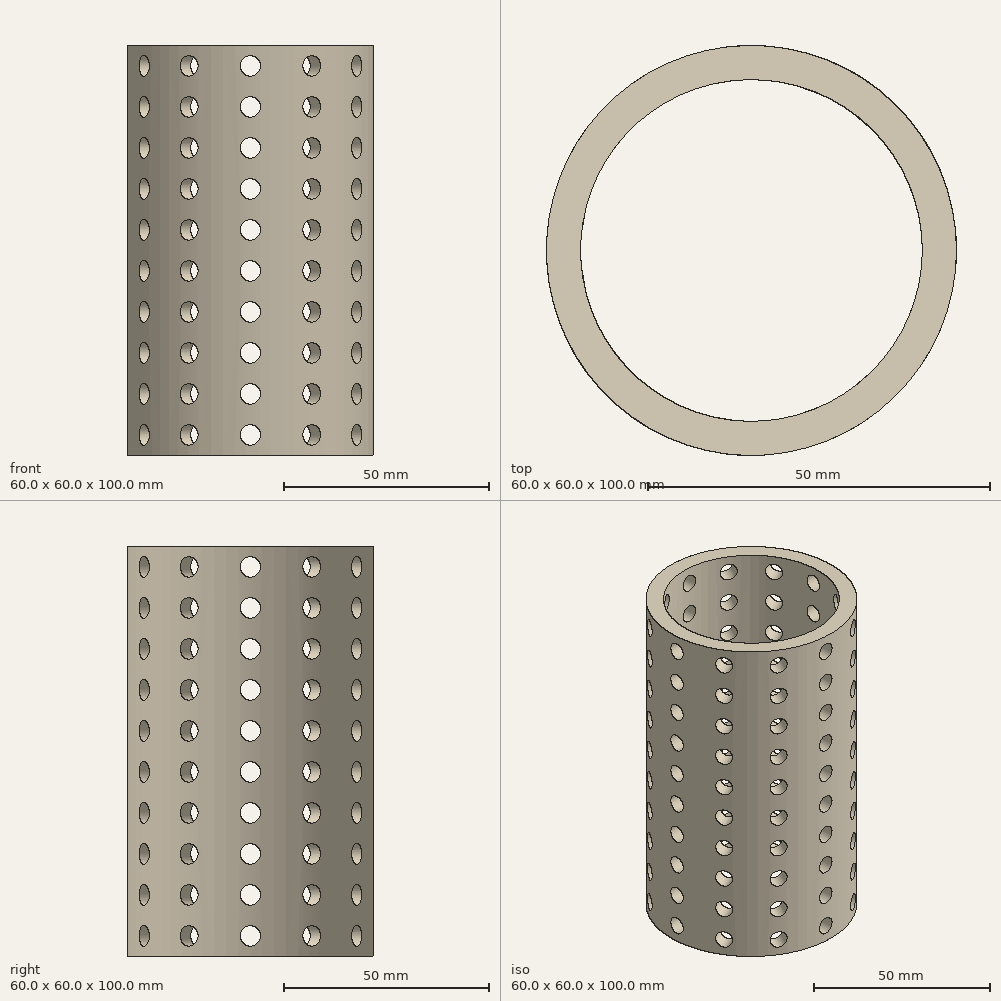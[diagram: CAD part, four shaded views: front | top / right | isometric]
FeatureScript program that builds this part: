
annotation { "Feature Type Name" : "Feature", "Feature Type Description" : "" }
export const myFeature = defineFeature(function(context is Context, id is Id, definition is map)
    precondition{}
    {
        {
            var Q0;
            Q0=qCreatedBy(makeId("Top.planeOp"),FACE);
            var sketch = newSketch(context, id + "F0", { "sketchPlane" : qUnion([Q0])});
            skCircle(sketch, "E0", {"center": v(0, 0) * mm, "radius": 30 * mm});
            skCircle(sketch, "E1", {"center": v(0, 0) * mm, "radius": 25 * mm});
            skSolve(sketch);
        }
        {
            var Q0;
            Q0=makeQuery(id+"F0.imprint","IMPRINT",FACE,{"disambiguationData":[TD([[makeQuery(id+"F0.imprint","IMPRINT",EDGE,{"derivedFrom":sQuery(id+"F0.wireOp",EDGE,"E0")}),1.0]])]});
            extrude(context, id + "F1", {"entities" : qUnion([Q0]), "depth" : 100 * mm});
        }
        {
            var Q0;
            Q0=qCreatedBy(makeId("Front.planeOp"),FACE);
            var sketch = newSketch(context, id + "F2", { "sketchPlane" : qUnion([Q0])});
            skCircle(sketch, "E2", {"center": v(0, 5) * mm, "radius": 2.5 * mm});
            skLineSegment(sketch, "E3", {"start": v(0, 0) * mm, "end": v(0, 99.71) * mm, "construction": true});
            skCircle(sketch, "E4.0.1.0", {"center": v(0, 15) * mm, "radius": 2.5 * mm});
            skCircle(sketch, "E4.0.2.0", {"center": v(0, 25) * mm, "radius": 2.5 * mm});
            skCircle(sketch, "E4.0.3.0", {"center": v(0, 35) * mm, "radius": 2.5 * mm});
            skCircle(sketch, "E4.0.4.0", {"center": v(0, 45) * mm, "radius": 2.5 * mm});
            skCircle(sketch, "E4.0.5.0", {"center": v(0, 55) * mm, "radius": 2.5 * mm});
            skCircle(sketch, "E4.0.6.0", {"center": v(0, 65) * mm, "radius": 2.5 * mm});
            skCircle(sketch, "E4.0.7.0", {"center": v(0, 75) * mm, "radius": 2.5 * mm});
            skCircle(sketch, "E4.0.8.0", {"center": v(0, 85) * mm, "radius": 2.5 * mm});
            skCircle(sketch, "E4.0.9.0", {"center": v(0, 95) * mm, "radius": 2.5 * mm});
            skLineSegment(sketch, "E4.direction1", {"start": v(0, 5) * mm, "end": v(25, 5) * mm, "construction": true});
            skLineSegment(sketch, "E4.direction2", {"start": v(0, 5) * mm, "end": v(0, 15) * mm, "construction": true});
            skSolve(sketch);
        }
        {
            var Q0;
            Q0 = qSketchRegion(id + "F2", true);
            extrude(context, id + "F3", {"entities" : qUnion([Q0]), "operationType" : NewBodyOperationType.REMOVE, "endBound" : BoundingType.THROUGH_ALL, "oppositeDirection" : true, "depth" : 25 * mm});
        }
        {
            var Q0;
            Q0=makeQuery(id+"F3.boolean.opBoolean","COPY",FACE,{"derivedFrom":makeQuery(id+"F3.opExtrude","SWEPT_FACE",FACE,{"disambiguationData":[OSD([sQuery(id+"F2.wireOp",EDGE,"E4.0.9.0")])]})});
            var Q1;
            Q1=makeQuery(id+"F3.boolean.opBoolean","COPY",FACE,{"derivedFrom":makeQuery(id+"F3.opExtrude","SWEPT_FACE",FACE,{"disambiguationData":[OSD([sQuery(id+"F2.wireOp",EDGE,"E4.0.8.0")])]})});
            var Q2;
            Q2=makeQuery(id+"F3.boolean.opBoolean","COPY",FACE,{"derivedFrom":makeQuery(id+"F3.opExtrude","SWEPT_FACE",FACE,{"disambiguationData":[OSD([sQuery(id+"F2.wireOp",EDGE,"E4.0.7.0")])]})});
            var Q3;
            Q3=makeQuery(id+"F3.boolean.opBoolean","COPY",FACE,{"derivedFrom":makeQuery(id+"F3.opExtrude","SWEPT_FACE",FACE,{"disambiguationData":[OSD([sQuery(id+"F2.wireOp",EDGE,"E4.0.6.0")])]})});
            var Q4;
            Q4=makeQuery(id+"F3.boolean.opBoolean","COPY",FACE,{"derivedFrom":makeQuery(id+"F3.opExtrude","SWEPT_FACE",FACE,{"disambiguationData":[OSD([sQuery(id+"F2.wireOp",EDGE,"E4.0.5.0")])]})});
            var Q5;
            Q5=makeQuery(id+"F3.boolean.opBoolean","COPY",FACE,{"derivedFrom":makeQuery(id+"F3.opExtrude","SWEPT_FACE",FACE,{"disambiguationData":[OSD([sQuery(id+"F2.wireOp",EDGE,"E4.0.4.0")])]})});
            var Q6;
            Q6=makeQuery(id+"F3.boolean.opBoolean","COPY",FACE,{"derivedFrom":makeQuery(id+"F3.opExtrude","SWEPT_FACE",FACE,{"disambiguationData":[OSD([sQuery(id+"F2.wireOp",EDGE,"E4.0.3.0")])]})});
            var Q7;
            Q7=makeQuery(id+"F3.boolean.opBoolean","COPY",FACE,{"derivedFrom":makeQuery(id+"F3.opExtrude","SWEPT_FACE",FACE,{"disambiguationData":[OSD([sQuery(id+"F2.wireOp",EDGE,"E4.0.2.0")])]})});
            var Q8;
            Q8=makeQuery(id+"F3.boolean.opBoolean","COPY",FACE,{"derivedFrom":makeQuery(id+"F3.opExtrude","SWEPT_FACE",FACE,{"disambiguationData":[OSD([sQuery(id+"F2.wireOp",EDGE,"E4.0.1.0")])]})});
            var Q9;
            Q9=makeQuery(id+"F3.boolean.opBoolean","COPY",FACE,{"derivedFrom":makeQuery(id+"F3.opExtrude","SWEPT_FACE",FACE,{"disambiguationData":[OSD([sQuery(id+"F2.wireOp",EDGE,"E2")])]})});
            var Q10;
            Q10=makeQuery(id+"F1.opExtrude","SWEPT_FACE",FACE,{"disambiguationData":[OSD([sQuery(id+"F0.wireOp",EDGE,"E1")])]});
            circularPattern(context, id + "F4", {"faces" : qUnion([Q0, Q1, Q2, Q3, Q4, Q5, Q6, Q7, Q8, Q9]), "axis" : qUnion([Q10]), "angle" : 30 * degree, "instanceCount" : 12, "patternType" : PatternType.FACE});
        }
    });
